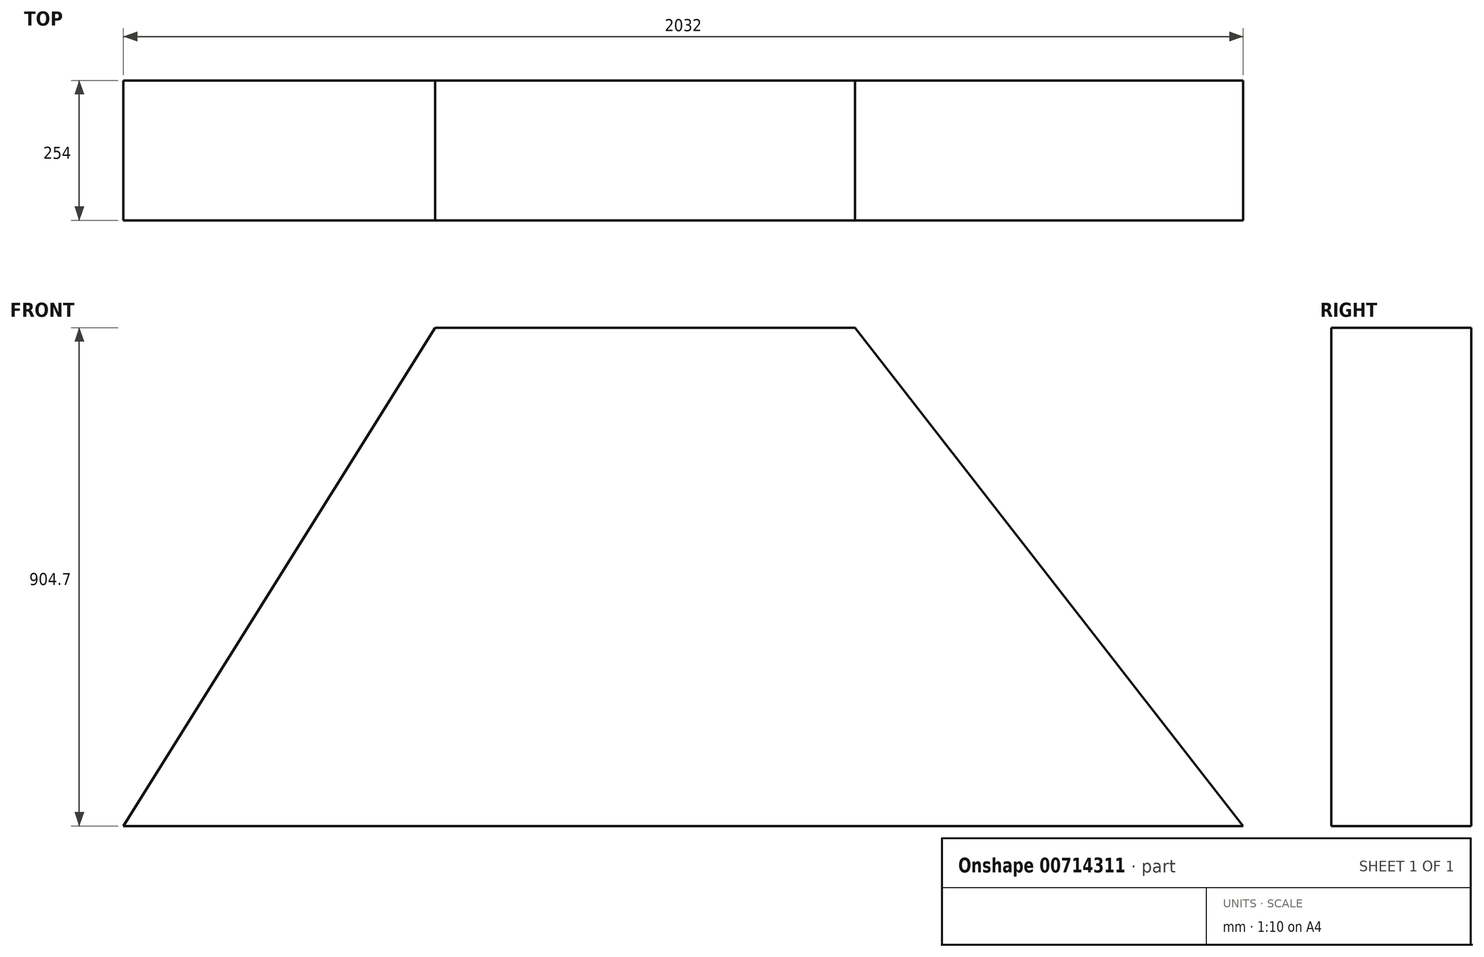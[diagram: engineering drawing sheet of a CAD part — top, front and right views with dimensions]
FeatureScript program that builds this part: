
annotation { "Feature Type Name" : "Feature", "Feature Type Description" : "" }
export const myFeature = defineFeature(function(context is Context, id is Id, definition is map)
    precondition{}
    {
        {
            var Q0;
            Q0=qCreatedBy(makeId("Front.planeOp"),FACE);
            var sketch = newSketch(context, id + "F0", { "sketchPlane" : qUnion([Q0])});
            skLineSegment(sketch, "E0", {"start": v(0, 0) * mm, "end": v(2032, 0) * mm});
            skLineSegment(sketch, "E1", {"start": v(2032, 0) * mm, "end": v(1327.32, 904.7) * mm});
            skLineSegment(sketch, "E2", {"start": v(1327.32, 904.7) * mm, "end": v(565.32, 904.7) * mm});
            skLineSegment(sketch, "E3", {"start": v(565.32, 904.7) * mm, "end": v(0, 0) * mm});
            skSolve(sketch);
        }
        {
            var Q0;
            Q0 = qSketchRegion(id + "F0", true);
            extrude(context, id + "F1", {"entities" : qUnion([Q0]), "depth" : 254 * mm, "offsetDistance" : 25.4 * mm});
        }
    });
